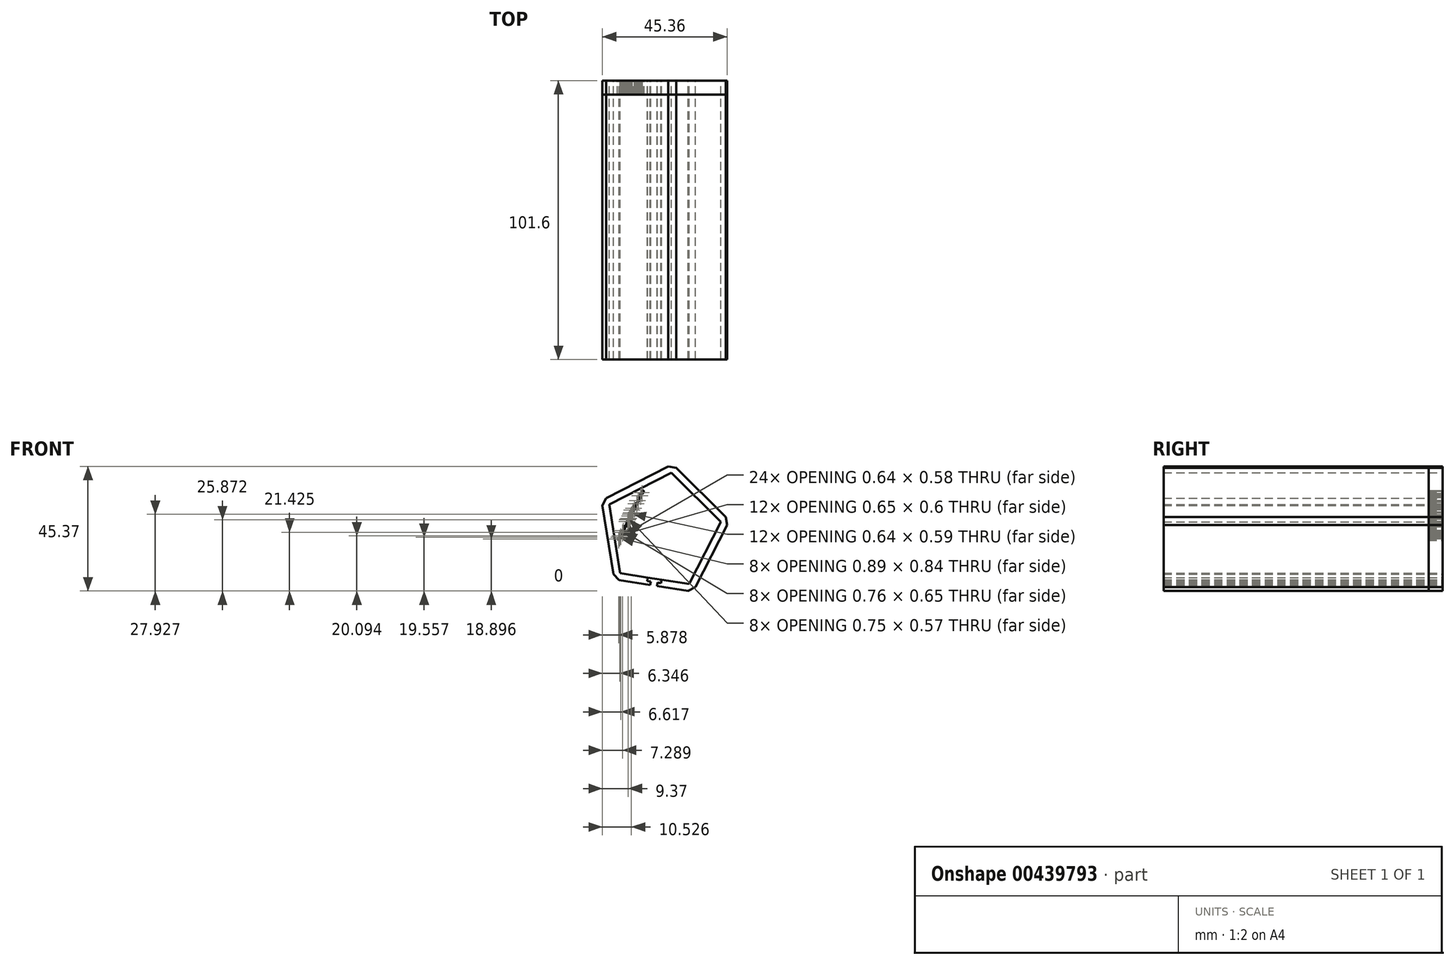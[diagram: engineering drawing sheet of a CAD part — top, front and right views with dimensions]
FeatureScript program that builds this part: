
annotation { "Feature Type Name" : "Feature", "Feature Type Description" : "" }
export const myFeature = defineFeature(function(context is Context, id is Id, definition is map)
    precondition{}
    {
        {
            var Q0;
            Q0=qCreatedBy(makeId("Front.planeOp"),FACE);
            var sketch = newSketch(context, id + "F0", { "sketchPlane" : qUnion([Q0])});
            skLineSegment(sketch, "E0", {"start": v(-27.51, 38.72) * mm, "end": v(-23.54, 13.64) * mm});
            skLineSegment(sketch, "E1", {"start": v(-23.54, 13.64) * mm, "end": v(1.55, 9.66) * mm});
            skLineSegment(sketch, "E2", {"start": v(1.55, 9.66) * mm, "end": v(13.08, 32.3) * mm});
            skLineSegment(sketch, "E3", {"start": v(13.08, 32.3) * mm, "end": v(-4.88, 50.26) * mm});
            skLineSegment(sketch, "E4", {"start": v(-4.88, 50.26) * mm, "end": v(-27.51, 38.72) * mm});
            skLineSegment(sketch, "E5", {"start": v(-27.51, 38.72) * mm, "end": v(-28.67, 40.99) * mm});
            skLineSegment(sketch, "E6", {"start": v(-4.88, 50.26) * mm, "end": v(-6.04, 52.52) * mm});
            skLineSegment(sketch, "E7", {"start": v(-28.67, 40.99) * mm, "end": v(-18.48, 46.18) * mm});
            skLineSegment(sketch, "E8", {"start": v(-6.04, 52.52) * mm, "end": v(-16.22, 47.33) * mm});
            skLineSegment(sketch, "E9", {"start": v(-4.88, 50.26) * mm, "end": v(-3.09, 52.05) * mm});
            skLineSegment(sketch, "E10", {"start": v(13.08, 32.3) * mm, "end": v(14.87, 34.1) * mm});
            skLineSegment(sketch, "E11", {"start": v(-3.09, 52.05) * mm, "end": v(5, 43.97) * mm});
            skLineSegment(sketch, "E12", {"start": v(14.87, 34.1) * mm, "end": v(6.8, 42.17) * mm});
            skLineSegment(sketch, "E13", {"start": v(-6.04, 52.52) * mm, "end": v(-3.09, 52.05) * mm});
            skLineSegment(sketch, "E14", {"start": v(13.08, 32.3) * mm, "end": v(15.34, 31.14) * mm});
            skLineSegment(sketch, "E15", {"start": v(15.34, 31.14) * mm, "end": v(10.15, 20.96) * mm});
            skLineSegment(sketch, "E16", {"start": v(1.55, 9.66) * mm, "end": v(3.8, 8.5) * mm});
            skLineSegment(sketch, "E17", {"start": v(3.8, 8.5) * mm, "end": v(9, 18.7) * mm});
            skLineSegment(sketch, "E18", {"start": v(14.87, 34.1) * mm, "end": v(15.34, 31.14) * mm});
            skLineSegment(sketch, "E19", {"start": v(-23.54, 13.64) * mm, "end": v(-23.94, 11.13) * mm});
            skLineSegment(sketch, "E20", {"start": v(-23.94, 11.13) * mm, "end": v(-12.65, 9.34) * mm});
            skLineSegment(sketch, "E21", {"start": v(-12.65, 9.34) * mm, "end": v(-12.45, 10.6) * mm});
            skLineSegment(sketch, "E22", {"start": v(-12.45, 10.6) * mm, "end": v(-13.7, 10.8) * mm});
            skLineSegment(sketch, "E23", {"start": v(-13.7, 10.8) * mm, "end": v(-13.5, 12.05) * mm});
            skLineSegment(sketch, "E24", {"start": v(1.55, 9.66) * mm, "end": v(1.15, 7.15) * mm});
            skLineSegment(sketch, "E25", {"start": v(1.15, 7.15) * mm, "end": v(-10.14, 8.94) * mm});
            skLineSegment(sketch, "E26", {"start": v(-10.14, 8.94) * mm, "end": v(-9.94, 10.2) * mm});
            skLineSegment(sketch, "E27", {"start": v(-9.94, 10.2) * mm, "end": v(-8.69, 10) * mm});
            skLineSegment(sketch, "E28", {"start": v(-8.69, 10) * mm, "end": v(-8.49, 11.25) * mm});
            skLineSegment(sketch, "E29", {"start": v(1.15, 7.15) * mm, "end": v(3.8, 8.5) * mm});
            skLineSegment(sketch, "E30", {"start": v(-27.51, 38.72) * mm, "end": v(-30.02, 38.33) * mm});
            skLineSegment(sketch, "E31", {"start": v(-30.02, 38.33) * mm, "end": v(-28.24, 27.04) * mm});
            skLineSegment(sketch, "E32", {"start": v(-28.67, 40.99) * mm, "end": v(-30.02, 38.33) * mm});
            skLineSegment(sketch, "E33", {"start": v(-23.54, 13.64) * mm, "end": v(-26.05, 13.24) * mm});
            skLineSegment(sketch, "E34", {"start": v(-26.05, 13.24) * mm, "end": v(-23.94, 11.13) * mm});
            skLineSegment(sketch, "E35", {"start": v(-26.05, 13.24) * mm, "end": v(-27.84, 24.53) * mm});
            skText(sketch, "E36", { "text": "Designed by Jefferson DeGrove Bishop", "fontName": "Arimo-Regular.ttf"});
            skLineSegment(sketch, "E37", {"start": v(5, 43.97) * mm, "end": v(6.8, 42.17) * mm});
            skLineSegment(sketch, "E38", {"start": v(10.15, 20.96) * mm, "end": v(9, 18.7) * mm});
            skLineSegment(sketch, "E39", {"start": v(-28.24, 27.04) * mm, "end": v(-27.84, 24.53) * mm});
            skLineSegment(sketch, "E40", {"start": v(-18.48, 46.18) * mm, "end": v(-16.22, 47.33) * mm});
            const initialGuessF0  = {"E36": [-0.02392, 0.02554, 0.44713, 0.89447, 0.00083]};
            skSetInitialGuess(sketch, initialGuessF0);
            skSolve(sketch);
        }
        {
            var Q0;
            {var subQ0=sQuery(id+"F0.wireOp",EDGE,"E5");Q0=makeQuery(id+"F0.imprint","IMPRINT",FACE,{"disambiguationData":[TD([[makeQuery(id+"F0.imprint","IMPRINT",EDGE,{"derivedFrom":subQ0}),-1.0]])]});}
            var Q1;
            {var subQ0=sQuery(id+"F0.wireOp",EDGE,"E6");Q1=makeQuery(id+"F0.imprint","IMPRINT",FACE,{"disambiguationData":[TD([[makeQuery(id+"F0.imprint","IMPRINT",EDGE,{"derivedFrom":subQ0}),1.0]])]});}
            var Q2;
            Q2=makeQuery(id+"F0.imprint","IMPRINT",FACE,{"disambiguationData":[TD([[makeQuery(id+"F0.imprint","IMPRINT",EDGE,{"derivedFrom":sQuery(id+"F0.wireOp",EDGE,"E6")}),-1.0]])]});
            var Q3;
            Q3=makeQuery(id+"F0.imprint","IMPRINT",FACE,{"disambiguationData":[TD([[makeQuery(id+"F0.imprint","IMPRINT",EDGE,{"derivedFrom":sQuery(id+"F0.wireOp",EDGE,"E3")}),-1.0]])]});
            var Q4;
            Q4=makeQuery(id+"F0.imprint","IMPRINT",FACE,{"disambiguationData":[TD([[makeQuery(id+"F0.imprint","IMPRINT",EDGE,{"derivedFrom":sQuery(id+"F0.wireOp",EDGE,"E10")}),-1.0]])]});
            var Q5;
            Q5=makeQuery(id+"F0.imprint","IMPRINT",FACE,{"disambiguationData":[TD([[makeQuery(id+"F0.imprint","IMPRINT",EDGE,{"derivedFrom":sQuery(id+"F0.wireOp",EDGE,"E2")}),-1.0]])]});
            var Q6;
            Q6=makeQuery(id+"F0.imprint","IMPRINT",FACE,{"disambiguationData":[TD([[makeQuery(id+"F0.imprint","IMPRINT",EDGE,{"derivedFrom":sQuery(id+"F0.wireOp",EDGE,"E5")}),1.0]])]});
            var Q7;
            {var subQ0=sQuery(id+"F0.wireOp",EDGE,"E30");Q7=makeQuery(id+"F0.imprint","IMPRINT",FACE,{"disambiguationData":[TD([[makeQuery(id+"F0.imprint","IMPRINT",EDGE,{"derivedFrom":subQ0}),1.0]])]});}
            var Q8;
            Q8=makeQuery(id+"F0.imprint","IMPRINT",FACE,{"disambiguationData":[TD([[makeQuery(id+"F0.imprint","IMPRINT",EDGE,{"derivedFrom":sQuery(id+"F0.wireOp",EDGE,"E19")}),-1.0]])]});
            var Q9;
            {var subQ0=sQuery(id+"F0.wireOp",EDGE,"E19");Q9=makeQuery(id+"F0.imprint","IMPRINT",FACE,{"disambiguationData":[TD([[makeQuery(id+"F0.imprint","IMPRINT",EDGE,{"derivedFrom":subQ0}),1.0]])]});}
            var Q10;
            {var subQ0=sQuery(id+"F0.wireOp",EDGE,"E33");Q10=makeQuery(id+"F0.imprint","IMPRINT",FACE,{"disambiguationData":[TD([[makeQuery(id+"F0.imprint","IMPRINT",EDGE,{"derivedFrom":subQ0}),-1.0]])]});}
            var Q11;
            Q11=makeQuery(id+"F0.imprint","IMPRINT",FACE,{"disambiguationData":[TD([[makeQuery(id+"F0.imprint","IMPRINT",EDGE,{"derivedFrom":sQuery(id+"F0.wireOp",EDGE,"E16")}),-1.0]])]});
            var Q12;
            {var subQ0=sQuery(id+"F0.wireOp",EDGE,"E24");Q12=makeQuery(id+"F0.imprint","IMPRINT",FACE,{"disambiguationData":[TD([[makeQuery(id+"F0.imprint","IMPRINT",EDGE,{"derivedFrom":subQ0}),-1.0]])]});}
            extrude(context, id + "F1", {"entities" : qUnion([Q0, Q1, Q2, Q3, Q4, Q5, Q6, Q7, Q8, Q9, Q10, Q11, Q12]), "depth" : 101.6 * mm});
        }
        {
            var Q0;
            Q0=qSketchRegion(id+"F0",true);
            extrude(context, id + "F2", {"entities" : qUnion([Q0]), "depth" : 5.08 * mm});
        }
    });
